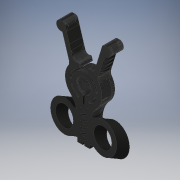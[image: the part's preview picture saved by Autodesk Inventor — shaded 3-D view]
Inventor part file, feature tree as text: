
AUTODESK INVENTOR PART (.ipt)
format: ipt  version: 2017 (Build 210142000, 142)  size: 3,618,816 bytes
history: native  units: in
note: dims shown in document units (in); Inventor stores cm internally (conversion verified against a paired STEP export)
features: other x2, extrude x2, sketch x2, plane x1, mirror x1
ambient origin geometry x8: Origin, YZ Plane, XZ Plane, XY Plane, X Axis, Y Axis, Z Axis, Center Point
bodies: Solid1 (feature_tree)
feature tree (8):
  other  "Chip_Bag_Clip_V7_Medium"
  other  "MeshFeature1"
  plane  "Work Plane1"
  extrude  "Extrusion1"  Depth=1.1811in TaperAngle=0.0deg
  extrude  "Extrusion3"  Depth=1.1811in TaperAngle=0.0deg
  mirror  "Mirror1"
  sketch  "Sketch1"  dims[d0=-0.2061in d1=0.58in d2=1.1811in d3=0.0in]
  sketch  "Sketch5"  dims[d4=1.1811in d5=0.0in d11=3.937in d12=0.0in]
